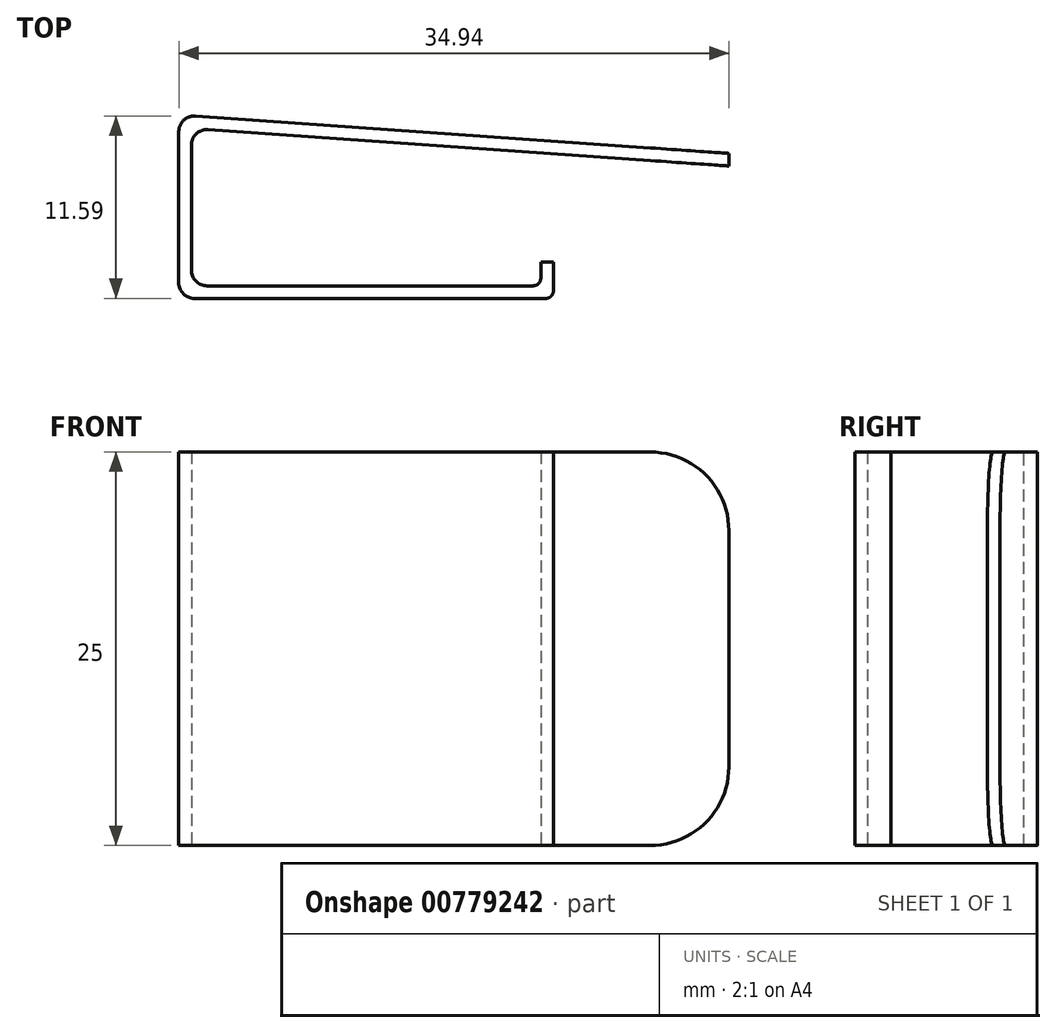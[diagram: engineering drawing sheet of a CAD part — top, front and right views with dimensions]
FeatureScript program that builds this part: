
annotation { "Feature Type Name" : "Feature", "Feature Type Description" : "" }
export const myFeature = defineFeature(function(context is Context, id is Id, definition is map)
    precondition{}
    {
        {
            var Q0;
            Q0=qCreatedBy(makeId("Top.planeOp"),FACE);
            var sketch = newSketch(context, id + "F0", { "sketchPlane" : qUnion([Q0])});
            skLineSegment(sketch, "E0", {"start": v(-12.94, 11.75) * mm, "end": v(10.06, 11.75) * mm});
            skLineSegment(sketch, "E1", {"start": v(10.06, 12.55) * mm, "end": v(-12.14, 12.55) * mm});
            skLineSegment(sketch, "E2", {"start": v(-12.14, 12.55) * mm, "end": v(-12.14, 22.55) * mm});
            skLineSegment(sketch, "E3", {"start": v(22, 20.16) * mm, "end": v(22, 20.96) * mm});
            skLineSegment(sketch, "E4", {"start": v(-12.94, 23.21) * mm, "end": v(-12.94, 11.75) * mm});
            skLineSegment(sketch, "E5", {"start": v(10.06, 12.55) * mm, "end": v(10.06, 14.05) * mm});
            skLineSegment(sketch, "E6", {"start": v(10.06, 14.05) * mm, "end": v(10.86, 14.05) * mm});
            skLineSegment(sketch, "E7", {"start": v(10.86, 14.05) * mm, "end": v(10.86, 11.75) * mm});
            skLineSegment(sketch, "E8", {"start": v(10.86, 11.75) * mm, "end": v(10.06, 11.75) * mm});
            skLineSegment(sketch, "E9", {"start": v(-12.14, 22.55) * mm, "end": v(22, 20.16) * mm});
            skLineSegment(sketch, "E10", {"start": v(-12.94, 23.21) * mm, "end": v(-12.94, 23.4) * mm});
            skLineSegment(sketch, "E11", {"start": v(-12.94, 23.4) * mm, "end": v(22, 20.96) * mm});
            skPoint(sketch, "E12.orphan", {"position": v(22, 22.55) * mm});
            skSolve(sketch);
        }
        {
            var Q0;
            Q0 = qSketchRegion(id + "F0", true);
            extrude(context, id + "F1", {"entities" : qUnion([Q0]), "depth" : 25 * mm, "offsetDistance" : 25 * mm});
        }
        {
            var Q0;
            Q0=makeQuery(id+"F1.opExtrude","CAP_EDGE",EDGE,{"disambiguationData":[OSD([sQuery(id+"F0.wireOp",EDGE,"E3")])],"isStart":false});
            var Q1;
            Q1=makeQuery(id+"F1.opExtrude","CAP_EDGE",EDGE,{"disambiguationData":[OSD([sQuery(id+"F0.wireOp",EDGE,"E3")])],"isStart":true});
            var Q2;
            Q2=makeQuery(id+"F1.opExtrude","CAP_EDGE",EDGE,{"disambiguationData":[OSD([sQuery(id+"F0.wireOp",EDGE,"fnczkInc-drZv-fcGi-AKD7-4SAqRtXQeUdC")])],"isStart":true});
            var Q3;
            Q3=makeQuery(id+"F1.opExtrude","CAP_EDGE",EDGE,{"disambiguationData":[OSD([sQuery(id+"F0.wireOp",EDGE,"fnczkInc-drZv-fcGi-AKD7-4SAqRtXQeUdC")])],"isStart":false});
            fillet(context, id + "F2", {"entities" : qUnion([Q0, Q1, Q2, Q3]), "radius" : 5 * mm, "tangentPropagation" : true, "allowEdgeOverflow" : false});
        }
        {
            var Q0;
            Q0=makeQuery(id+"F1.opExtrude","SWEPT_EDGE",EDGE,{"disambiguationData":[OSD([sQuery(id+"F0.wireOp",EDGE,"E0"),sQuery(id+"F0.wireOp",EDGE,"E4")])]});
            var Q1;
            Q1=makeQuery(id+"F1.opExtrude","SWEPT_EDGE",EDGE,{"disambiguationData":[OSD([sQuery(id+"F0.wireOp",EDGE,"E1"),sQuery(id+"F0.wireOp",EDGE,"E2")])]});
            var Q2;
            Q2=makeQuery(id+"F1.opExtrude","SWEPT_EDGE",EDGE,{"disambiguationData":[OSD([sQuery(id+"F0.wireOp",EDGE,"E2"),sQuery(id+"F0.wireOp",EDGE,"NX4fU2IB-74GT-vJKc-VbzI-sAVCscqTqjp3")])]});
            var Q3;
            Q3=makeQuery(id+"F1.opExtrude","SWEPT_EDGE",EDGE,{"disambiguationData":[OSD([sQuery(id+"F0.wireOp",EDGE,"BDzU2zpZ-zXeU-31Oa-3r9x-caPweCMrj82Q"),sQuery(id+"F0.wireOp",EDGE,"E4")])]});
            var Q4;
            Q4=makeQuery(id+"F1.opExtrude","SWEPT_EDGE",EDGE,{"disambiguationData":[OSD([sQuery(id+"F0.wireOp",EDGE,"E10"),sQuery(id+"F0.wireOp",EDGE,"E11")])]});
            fillet(context, id + "F3", {"entities" : qUnion([Q0, Q1, Q2, Q3, Q4]), "radius" : 1 * mm, "tangentPropagation" : true, "allowEdgeOverflow" : false});
        }
        {
            var Q0;
            Q0=makeQuery(id+"F1.opExtrude","SWEPT_EDGE",EDGE,{"disambiguationData":[OSD([sQuery(id+"F0.wireOp",EDGE,"E7"),sQuery(id+"F0.wireOp",EDGE,"E8")])]});
            var Q1;
            Q1=makeQuery(id+"F1.opExtrude","SWEPT_EDGE",EDGE,{"disambiguationData":[OSD([sQuery(id+"F0.wireOp",EDGE,"E1"),sQuery(id+"F0.wireOp",EDGE,"E5")])]});
            fillet(context, id + "F4", {"entities" : qUnion([Q0, Q1]), "radius" : 0.5 * mm, "tangentPropagation" : true, "allowEdgeOverflow" : false});
        }
    });
